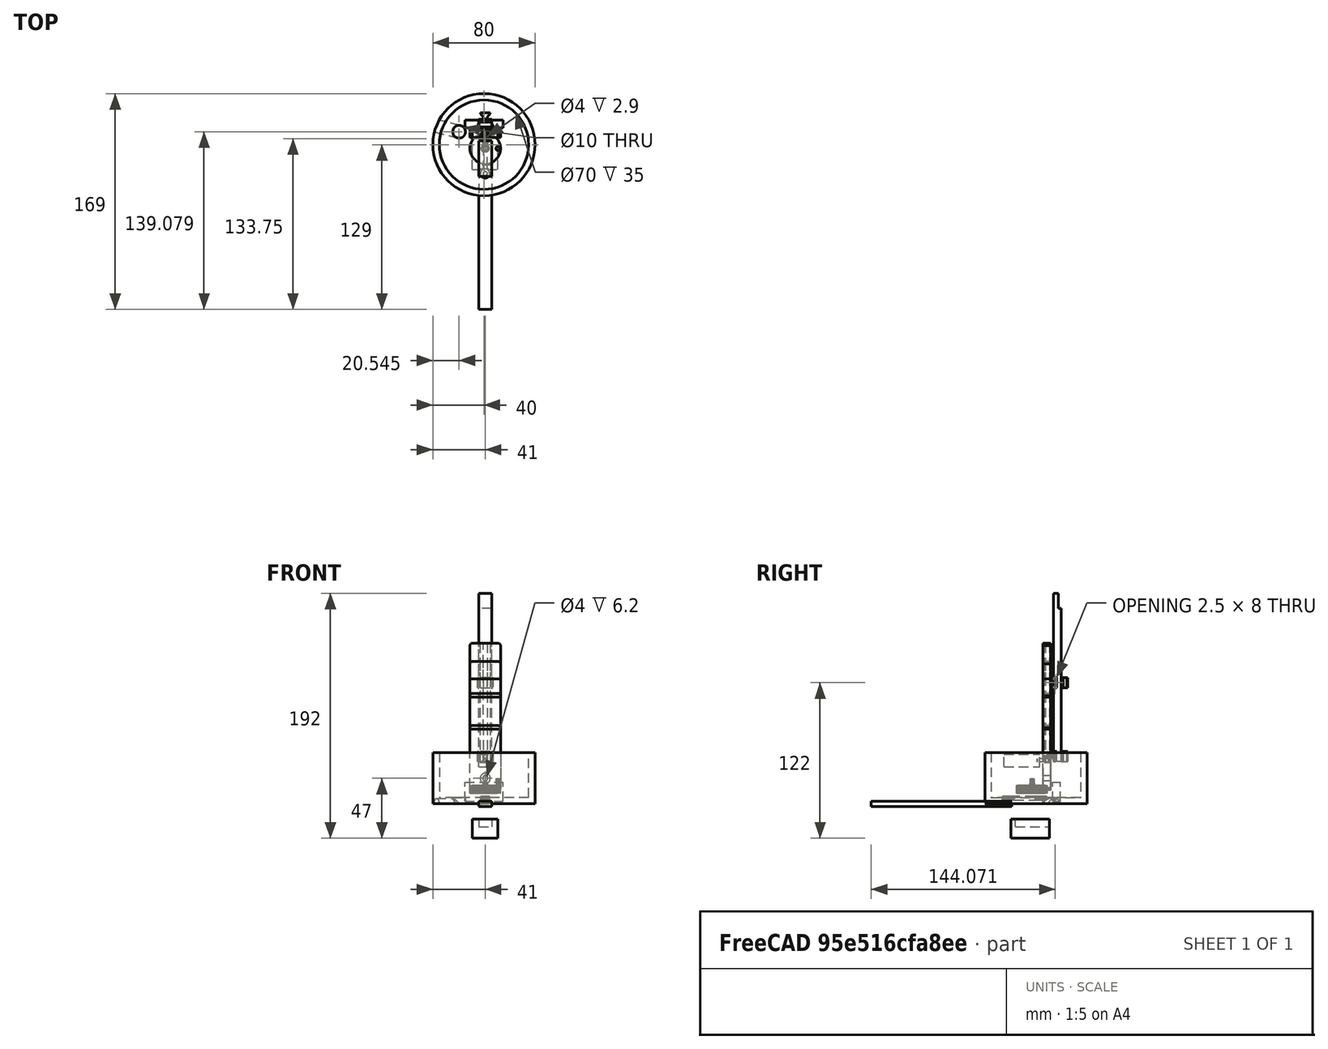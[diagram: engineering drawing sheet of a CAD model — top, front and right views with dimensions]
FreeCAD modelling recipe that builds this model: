
FCSTD DOCUMENT  (FreeCAD 1.0R39319 (Git))
Label: unicorn_lamp
License: All rights reserved
LicenseURL: https://en.wikipedia.org/wiki/All_rights_reserved
objects: Part::FeaturePython×14, Part::Cylinder×12, Part::Feature×10, App::Part×9, Part::Cut×9, Part::Box×7, Part::Plane×7, Mesh::Feature×5, Part::Fuse×3, Part::MultiFuse×2, PartDesign::Body×1, PartDesign::AdditiveCylinder×1, App::DocumentObjectGroup×1
note: 68 computed .brp shape members not serialized (recipe doc carries the construction recipe); baked Part::Feature solids carry a one-line shape summary decoded from their .brp

FEATURE [Mesh::Feature] Unicorn_Lamp__3_  label="outer_mesh_with_holes"
FEATURE [PartDesign::Body] Body  label="outer_cylinder"
  AllowCompound = false
  Origin = -> Origin001
FEATURE [PartDesign::AdditiveCylinder] Cylinder
  Angle = 360
  AttacherType = Attacher::AttachEngine3D
  AttachmentSupport = -> [Origin001]
  FirstAngle = 0
  Height = 40
  Placement = pos=(-1,3,-10) rot=(0,0,1;0rad)
  Radius = 40
  Refine = true
  SecondAngle = 0
  Suppressed = false
FEATURE [Mesh::Feature] rod  label="crank_rod_mesh"
  Placement = pos=(-1.3e-15,-6,-7) rot=(0,0,-1;1.5708rad)
FEATURE [Mesh::Feature] crank_clearence_fit  label="crank_clearence_fit_mesh"
  Placement = pos=(0,16,-13) rot=(0,0,1;0rad)
FEATURE [Mesh::Feature] base  label="crank_base_mesh"
  Placement = pos=(0,0,-20) rot=(0,0,1;0rad)
FEATURE [Mesh::Feature] slider_clearence_fit  label="crank_slider_mesh"
  Placement = pos=(0,-20,-19) rot=(0,0,1;0rad)
FEATURE [Part::Box] Box001  label="crank_to_base_mount"
  AttacherType = Attacher::AttachEngine3D
  Height = 15
  Length = 30
  Placement = pos=(-16,16.25,-8) rot=(0,0,1;0rad)
  Width = 6
FEATURE [Part::Box] Box004  label="gear_box001"
  AttacherType = Attacher::AttachEngine3D
  Height = 10
  Length = 10
  Placement = pos=(-5,-22,19) rot=(0,0,1;0rad)
  Width = 28
FEATURE [Part::Cylinder] Cylinder002  label="shaft001"
  Angle = 360
  AttacherType = Attacher::AttachEngine3D
  FirstAngle = 0
  Height = 9
  Placement = pos=(0,4,24) rot=(1,0,0;4.71239rad)
  Radius = 1.25
  SecondAngle = 0
FEATURE [App::Part] Part002  label="motor_for_fit001"
  Group = -> [Box004,Cylinder002]
  Origin = -> Origin003
  Placement = pos=(0,6,20) rot=(0,0,1;0rad)
FEATURE [Part::Cylinder] Cylinder003
  Angle = 360
  AttacherType = Attacher::AttachEngine3D
  FirstAngle = 0
  Height = 40
  Placement = pos=(-1,3,-5) rot=(0,0,1;0rad)
  Radius = 35
  SecondAngle = 0
FEATURE [Part::Cut] Cut001  label="base_cup"
  Base = -> Cylinder
  Tool = -> Cylinder003
FEATURE [App::Part] Part005  label="crank_mount"
  Group = -> [Box001]
  Origin = -> Origin006
  Placement = pos=(3.8e-15,30.75,0) rot=(0,0,1;3.14159rad)
FEATURE [Part::Box] Box005  label="gear_box002"
  AttacherType = Attacher::AttachEngine3D
  Height = 10
  Length = 10
  Placement = pos=(-5,-24.5,16) rot=(0,0,1;0rad)
  Width = 28
FEATURE [Part::Box] Box006  label="motor_to_base_mount001"
  AttacherType = Attacher::AttachEngine3D
  Height = 15
  Length = 20
  Placement = pos=(-10,-28,7) rot=(0,0,1;0rad)
  Width = 30
FEATURE [Part::Cut] Cut002  label="motor_mount_cutout001"
  Base = -> Box006
  Placement = pos=(0,11.5,-44) rot=(0,0,1;0rad)
  Tool = -> Box005
FEATURE [App::Part] Part006  label="motor_mount001"
  Group = -> [Box006,Box005,Cut002]
  Origin = -> Origin007
  Placement = pos=(0,-6.75,32) rot=(0,0,1;0rad)
FEATURE [Part::Box] Box  label="crank_column"
  AttacherType = Attacher::AttachEngine3D
  Height = 110
  Length = 10
  Placement = pos=(-5,-16,-12) rot=(1,0,0;1.5708rad)
  Width = 4
FEATURE [App::Part] Part001  label="crank_for_fit"
  Group = -> [crank_clearence_fit,rod,base,slider_clearence_fit,Box]
  Origin = -> Origin002
  Placement = pos=(-1.8e-15,28.75,60) rot=(-1,0,0;1.5708rad)
FEATURE [App::Part] Part003  label="sub_assembly_for_fit"
  Group = -> [Part001,Part002]
  Origin = -> Origin004
  Placement = pos=(0,0,-34) rot=(0,0,1;0rad)
FEATURE [Part::Box] Box011  label="crank_column002"
  AttacherType = Attacher::AttachEngine3D
  Height = 120
  Length = 10
  Placement = pos=(-5,-16,-13.75) rot=(1,0,0;1.5708rad)
  Width = 6
FEATURE [Part::Feature] slider_clearence_fit002_solid  label="slider_clearence_fit002 (Solid)"
  shape: bbox 12 x 8 x 16.18 mm, 518 faces (baked)
FEATURE [Part::MultiFuse] Fusion  label="crank_slider_with_column_fused"
  Placement = pos=(-1.1e-15,9,7) rot=(0,-0.707107,0.707107;3.14159rad)
  Shapes = -> [slider_clearence_fit002_solid,Box011]
FEATURE [Part::Feature] base001_solid  label="crank_base_shape (Solid)"
  shape: bbox 24 x 6.2 x 50.7 mm, 492 faces (baked)
FEATURE [Part::Cylinder] Cylinder006
  Angle = 360
  AttacherType = Attacher::AttachEngine3D
  FirstAngle = 0
  Height = 20
  Placement = pos=(-20.3237,13.1165,-15.5399) rot=(-0.026127,0.061891,0.997741;6.02987rad)
  Radius = 5
  SecondAngle = 0
FEATURE [Part::Cylinder] Cylinder007
  Angle = 360
  AttacherType = Attacher::AttachEngine3D
  FirstAngle = 0
  Height = 20
  Placement = pos=(-20.4013,13.0948,-10.7906) rot=(0.120746,0.984202,0.129484;4.69816rad)
  Radius = 5
  SecondAngle = 0
FEATURE [Part::MultiFuse] Fusion002  label="power_cable_hole"
  Shapes = -> [Cylinder007,Cylinder006]
FEATURE [Part::Cut] Cut  label="base_cup_with_hole"
  Base = -> Cut001
  Tool = -> Fusion002
FEATURE [Part::Feature] crank_clearence_fit002
  Placement = pos=(0,-16,11.5) rot=(0,0,1;0rad)
  shape: bbox 24 x 23.99 x 11 mm, 1138 faces, 0 solids (baked)
FEATURE [Part::Cylinder] Cylinder008
  Angle = 360
  AttacherType = Attacher::AttachEngine3D
  FirstAngle = 0
  Height = 4
  Placement = pos=(0,0,-1.5) rot=(0,0,1;0rad)
  Radius = 2
  SecondAngle = 0
FEATURE [Part::Feature] crank_clearence_fit002_solid  label="crank_clearence_fit002 (Solid)"
  shape: bbox 24 x 23.99 x 11 mm, 1138 faces (baked)
FEATURE [Part::Fuse] Fusion003  label="fused_crank_to_cut"
  Base = -> Cylinder008
  Tool = -> crank_clearence_fit002_solid
FEATURE [Part::Cylinder] Cylinder009
  Angle = 360
  AttacherType = Attacher::AttachEngine3D
  FirstAngle = 0
  Height = 6
  Radius = 1.9
  SecondAngle = 0
FEATURE [Part::Plane] Plane
  AttacherType = Attacher::AttachEngine3D
  Length = 10
  Placement = pos=(-4.75,-1.25,8.5) rot=(1,0,0;4.71239rad)
  Width = 10
FEATURE [Part::Cylinder] Cylinder010
  Angle = 360
  AttacherType = Attacher::AttachEngine3D
  FirstAngle = 0
  Height = 6
  Radius = 1.7
  SecondAngle = 0
FEATURE [Part::Plane] Plane001
  AttacherType = Attacher::AttachEngine3D
  Length = 10
  Placement = pos=(-4.75,-1.25,8.5) rot=(1,0,0;4.71239rad)
  Width = 10
FEATURE [Part::FeaturePython] Slice001  # WARN: FeaturePython — macro-defined, semantics opaque (R4)
  Base = -> Cylinder010
  Mode = 1
  Tolerance = 0
  Tools = -> [Plane001]
FEATURE [Part::Cylinder] Cylinder011  label="larger_hole"
  Angle = 360
  AttacherType = Attacher::AttachEngine3D
  FirstAngle = 0
  Height = 10
  Placement = pos=(0,32.75,10) rot=(1,0,0;1.5708rad)
  Radius = 2
  SecondAngle = 0
FEATURE [Part::Cut] Cut006  label="crank_base_larger_hole"
  Base = -> base001_solid
  Placement = pos=(4.6e-15,37.5,0) rot=(0,0,1;3.14159rad)
  Tool = -> Cylinder011
FEATURE [Part::Feature] rod001
  shape: bbox 7.193 x 34.54 x 2.9 mm, 772 faces, 0 solids (baked)
FEATURE [Part::Cylinder] Cylinder012
  Angle = 360
  AttacherType = Attacher::AttachEngine3D
  FirstAngle = 0
  Height = 10
  Placement = pos=(0,7.75,-7) rot=(0,0,1;0rad)
  Radius = 2
  SecondAngle = 0
FEATURE [Part::Feature] Part_solid  label="rod_bigger_holes (Solid)"
  shape: bbox 7.193 x 34.54 x 2.9 mm, 772 faces (baked)
FEATURE [Part::Cut] Cut007
  Base = -> Part_solid
  Tool = -> Cylinder012
FEATURE [App::Part] Part  label="rod_bigger_holes"
  Group = -> [rod001,Cylinder012,Part_solid,Cut007]
  Origin = -> Origin
FEATURE [Part::Plane] Plane002
  AttacherType = Attacher::AttachEngine3D
  Length = 10
  Placement = pos=(-4.75,1.35,8.5) rot=(1,0,0;4.71239rad)
  Width = 10
FEATURE [Part::FeaturePython] Slice002  # WARN: FeaturePython — macro-defined, semantics opaque (R4)
  Base = -> Slice001
  Mode = 1
  Tolerance = 0
  Tools = -> [Plane002]
FEATURE [Part::FeaturePython] Slice002_child0  label="double_flat_hole"  # WARN: FeaturePython — macro-defined, semantics opaque (R4)
  Base = -> Slice002
  FilterType = 1
  Invert = false
  OverrideMaxVal = 0
  Placement = pos=(0,0,-1.5) rot=(0,0,1;0rad)
  WindowFrom = 80
  WindowTo = 100
  items = 0
FEATURE [Part::FeaturePython] Slice002_child1  label="Slice002.1"  # WARN: FeaturePython — macro-defined, semantics opaque (R4)
  Base = -> Slice002
  FilterType = 1
  Invert = false
  OverrideMaxVal = 0
  WindowFrom = 80
  WindowTo = 100
  items = 1
FEATURE [Part::FeaturePython] Slice002_child2  label="Slice002.2"  # WARN: FeaturePython — macro-defined, semantics opaque (R4)
  Base = -> Slice002
  FilterType = 1
  Invert = false
  OverrideMaxVal = 0
  WindowFrom = 80
  WindowTo = 100
  items = 2
FEATURE [App::DocumentObjectGroup] GrExplode_Slice002  label="square_hole_fillers_do_not_delete"
  Group = -> [Slice002_child1,Slice002_child2]
FEATURE [Part::Cut] Cut008  label="crank_double_flat_hole"
  Base = -> Fusion003
  Tool = -> Slice002_child0
FEATURE [Part::Cylinder] Cylinder013  label="larger_hole001"
  Angle = 360
  AttacherType = Attacher::AttachEngine3D
  FirstAngle = 0
  Height = 10
  Placement = pos=(0,32.75,10) rot=(1,0,0;1.5708rad)
  Radius = 2
  SecondAngle = 0
FEATURE [Part::Feature] base001_solid001  label="crank_base_shape (Solid)001"
  shape: bbox 24 x 6.2 x 50.7 mm, 492 faces (baked)
FEATURE [Part::Cut] Cut009  label="crank_base_larger_hole001"
  Base = -> base001_solid001
  Placement = pos=(4.6e-15,37.5,57.75) rot=(0,0,1;3.14159rad)
  Tool = -> Cylinder013
FEATURE [Part::Plane] Plane003
  AttacherType = Attacher::AttachEngine3D
  Length = 40
  Placement = pos=(-20,7,81) rot=(0,0,1;0rad)
  Width = 10
FEATURE [Part::FeaturePython] Slice003  # WARN: FeaturePython — macro-defined, semantics opaque (R4)
  Base = -> Cut009
  Mode = 1
  Tolerance = 0
  Tools = -> [Plane003]
FEATURE [Part::FeaturePython] Slice003_child1  label="Slice003.1"  # WARN: FeaturePython — macro-defined, semantics opaque (R4)
  Base = -> Slice003
  FilterType = 1
  Invert = false
  OverrideMaxVal = 0
  Placement = pos=(0,0,-32.5) rot=(0,0,1;0rad)
  WindowFrom = 80
  WindowTo = 100
  items = 1
FEATURE [Part::Cylinder] Cylinder014  label="larger_hole002"
  Angle = 360
  AttacherType = Attacher::AttachEngine3D
  FirstAngle = 0
  Height = 10
  Placement = pos=(0,32.75,10) rot=(1,0,0;1.5708rad)
  Radius = 2
  SecondAngle = 0
FEATURE [Part::Plane] Plane004
  AttacherType = Attacher::AttachEngine3D
  Length = 40
  Placement = pos=(-20,7,81) rot=(0,0,1;0rad)
  Width = 10
FEATURE [Part::Feature] base001_solid002  label="crank_base_shape (Solid)002"
  shape: bbox 24 x 6.2 x 50.7 mm, 492 faces (baked)
FEATURE [Part::Cut] Cut010  label="crank_base_larger_hole002"
  Base = -> base001_solid002
  Placement = pos=(4.6e-15,37.5,57.75) rot=(0,0,1;3.14159rad)
  Tool = -> Cylinder014
FEATURE [Part::FeaturePython] Slice004  # WARN: FeaturePython — macro-defined, semantics opaque (R4)
  Base = -> Cut010
  Mode = 1
  Tolerance = 0
  Tools = -> [Plane004]
FEATURE [Part::FeaturePython] Slice003_child002  label="Slice003.002"  # WARN: FeaturePython — macro-defined, semantics opaque (R4)
  Base = -> Slice004
  FilterType = 1
  Invert = false
  OverrideMaxVal = 0
  Placement = pos=(0,0,-7.5) rot=(0,0,1;0rad)
  WindowFrom = 80
  WindowTo = 100
  items = 1
FEATURE [Part::Cylinder] Cylinder018  label="larger_hole006"
  Angle = 360
  AttacherType = Attacher::AttachEngine3D
  FirstAngle = 0
  Height = 10
  Placement = pos=(0,32.75,10) rot=(1,0,0;1.5708rad)
  Radius = 2
  SecondAngle = 0
FEATURE [Part::Plane] Plane008
  AttacherType = Attacher::AttachEngine3D
  Length = 40
  Placement = pos=(-20,7,81) rot=(0,0,1;0rad)
  Width = 10
FEATURE [Part::Feature] base001_solid006  label="crank_base_shape (Solid)006"
  shape: bbox 24 x 6.2 x 50.7 mm, 492 faces (baked)
FEATURE [Part::Cut] Cut012  label="crank_base_larger_hole004"
  Base = -> base001_solid006
  Placement = pos=(4.6e-15,37.5,57.75) rot=(0,0,1;3.14159rad)
  Tool = -> Cylinder018
FEATURE [Part::FeaturePython] Slice006  # WARN: FeaturePython — macro-defined, semantics opaque (R4)
  Base = -> Cut012
  Mode = 1
  Tolerance = 0
  Tools = -> [Plane008]
FEATURE [Part::FeaturePython] Slice003_child004  label="Slice003.004"  # WARN: FeaturePython — macro-defined, semantics opaque (R4)
  Base = -> Slice006
  FilterType = 1
  Invert = false
  OverrideMaxVal = 0
  Placement = pos=(0,0,6.75) rot=(0,0,1;0rad)
  WindowFrom = 80
  WindowTo = 100
  items = 1
FEATURE [App::Part] Part004  label="lamp_base"
  Group = -> [Body,Part005,Part006,Cylinder006,Cylinder,Cylinder003,Cut001,Fusion002,Cylinder007,Cut,base001_solid,Cylinder011,Cut006,Slice003,Cylinder013,Cut009,base001_solid001,Plane003,Slice003_child1,Plane004,base001_solid002,Cut010,Cylinder014,Slice004,Slice003_child004,Slice003_child002,base001_solid006,Cut012,Slice006,Cylinder018,Plane008]
  Origin = -> Origin005
FEATURE [Part::Feature] slider_clearence_fit002_solid001  label="slider_clearence_fit002 (Solid)001"
  Placement = pos=(0,9,105) rot=(1,0,0;1.5708rad)
  shape: bbox 12 x 16.18 x 8 mm, 518 faces (baked)
FEATURE [Part::Fuse] Fusion004
  Base = -> Fusion
  Tool = -> slider_clearence_fit002_solid001
FEATURE [Part::Plane] Plane009
  AttacherType = Attacher::AttachEngine3D
  Length = 10
  Placement = pos=(-5,16.75,80) rot=(-1,0,0;4.71239rad)
  Width = 10
FEATURE [Part::FeaturePython] Slice007  # WARN: FeaturePython — macro-defined, semantics opaque (R4)
  Base = -> Fusion004
  Mode = 1
  Tolerance = 0
  Tools = -> [Plane009]
FEATURE [Part::FeaturePython] Slice007_child0  label="slider_double_support_final"  # WARN: FeaturePython — macro-defined, semantics opaque (R4)
  Base = -> Slice007
  FilterType = 1
  Invert = false
  OverrideMaxVal = 0
  WindowFrom = 80
  WindowTo = 100
  items = 0
FEATURE [Part::FeaturePython] Slice  label="square_hole_slice_do_not_delete"  # WARN: FeaturePython — macro-defined, semantics opaque (R4)
  Base = -> Cylinder009
  Mode = 1
  Tolerance = 0
  Tools = -> [Plane]
FEATURE [App::Part] Part010  label="crank_with_flat_hole"
  Group = -> [crank_clearence_fit002,Slice002_child0,Slice002_child2,Slice002,Cylinder008,crank_clearence_fit002_solid,Fusion003,Cylinder010,Plane001,Slice001,Plane002,Slice002_child1,Cut008,Cylinder009,Plane,Slice,GrExplode_Slice002]
  Origin = -> Origin012
FEATURE [Part::Box] Box012  label="Cube"
  AttacherType = Attacher::AttachEngine3D
  Height = 15
  Length = 10
  Placement = pos=(-5,16.75,140) rot=(0,0,1;0rad)
  Width = 4
FEATURE [Part::Fuse] Fusion005
  Base = -> Slice007_child0
  Tool = -> Box012
FEATURE [App::Part] Part011  label="slider_double_support"
  Group = -> [Box011,slider_clearence_fit002_solid,Fusion,slider_clearence_fit002_solid001,Fusion004,Plane009,Slice007,Slice007_child0,Box012,Fusion005]
  Origin = -> Origin013
